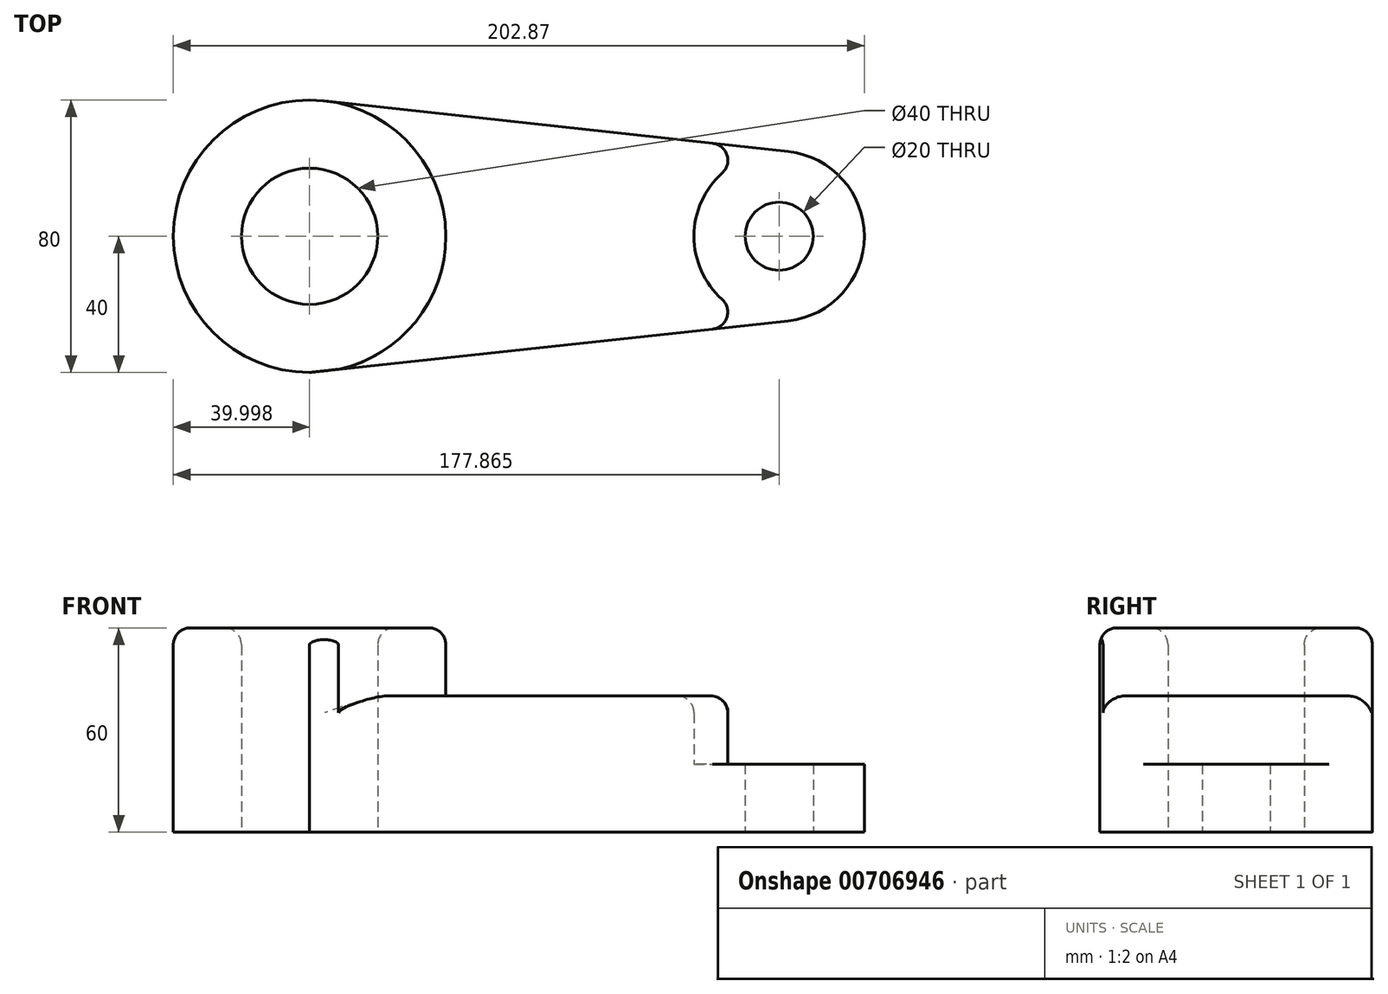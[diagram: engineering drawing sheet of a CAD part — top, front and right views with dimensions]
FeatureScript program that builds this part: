
annotation { "Feature Type Name" : "Feature", "Feature Type Description" : "" }
export const myFeature = defineFeature(function(context is Context, id is Id, definition is map)
    precondition{}
    {
        {
            var Q0;
            Q0=qCreatedBy(makeId("Top.planeOp"),FACE);
            var sketch = newSketch(context, id + "F0", { "sketchPlane" : qUnion([Q0])});
            skCircle(sketch, "E0", {"center": v(-69.3, 0) * mm, "radius": 40 * mm});
            skCircle(sketch, "E1", {"center": v(-69.3, 0) * mm, "radius": 20 * mm});
            skCircle(sketch, "E2", {"center": v(68.58, 0) * mm, "radius": 25 * mm});
            skCircle(sketch, "E3", {"center": v(68.58, 0) * mm, "radius": 10 * mm});
            skLineSegment(sketch, "E4", {"start": v(-64.94, 39.76) * mm, "end": v(71.3, 24.85) * mm});
            skLineSegment(sketch, "E5", {"start": v(-69.3, -40) * mm, "end": v(71.25, -24.86) * mm});
            skSolve(sketch);
        }
        {
            var Q0;
            Q0=makeQuery(id+"F0.imprint","IMPRINT",FACE,{"disambiguationData":[TD([[makeQuery(id+"F0.imprint","IMPRINT",EDGE,{"derivedFrom":sQuery(id+"F0.wireOp",EDGE,"E1")}),-1.0]])]});
            extrude(context, id + "F1", {"entities" : qUnion([Q0]), "depth" : 60 * mm, "offsetDistance" : 25 * mm});
        }
        {
            var Q0;
            {var subQ0=sQuery(id+"F0.wireOp",EDGE,"E4");Q0=makeQuery(id+"F0.imprint","IMPRINT",FACE,{"disambiguationData":[TD([[makeQuery(id+"F0.imprint","IMPRINT",EDGE,{"derivedFrom":subQ0}),-1.0]])]});}
            extrude(context, id + "F2", {"entities" : qUnion([Q0]), "operationType" : NewBodyOperationType.ADD, "depth" : 40 * mm, "offsetDistance" : 25 * mm});
        }
        {
            var Q0;
            Q0=makeQuery(id+"F0.imprint","IMPRINT",FACE,{"disambiguationData":[TD([[makeQuery(id+"F0.imprint","IMPRINT",EDGE,{"derivedFrom":sQuery(id+"F0.wireOp",EDGE,"E3")}),-1.0]])]});
            extrude(context, id + "F3", {"entities" : qUnion([Q0]), "operationType" : NewBodyOperationType.ADD, "depth" : 20 * mm, "offsetDistance" : 25 * mm});
        }
        {
            var Q0;
            Q0=makeQuery(id+"F1.opExtrude","CAP_EDGE",EDGE,{"disambiguationData":[OSD([sQuery(id+"F0.wireOp",EDGE,"E1")])],"isStart":false});
            var Q1;
            Q1=makeQuery(id+"F1.opExtrude","CAP_EDGE",EDGE,{"disambiguationData":[OSD([sQuery(id+"F0.wireOp",EDGE,"E0")])],"isStart":false});
            var Q2;
            Q2=makeQuery(id+"F2.opExtrude","CAP_EDGE",EDGE,{"disambiguationData":[OSD([sQuery(id+"F0.wireOp",EDGE,"E5")])],"isStart":false});
            var Q3;
            Q3=makeQuery(id+"F2.opExtrude","CAP_EDGE",EDGE,{"disambiguationData":[OSD([sQuery(id+"F0.wireOp",EDGE,"E4")])],"isStart":false});
            var Q4;
            Q4=makeQuery(id+"F2.opExtrude","CAP_EDGE",EDGE,{"disambiguationData":[OSD([sQuery(id+"F0.wireOp",EDGE,"E2")])],"isStart":false});
            var Q5;
            {var subQ0=sQuery(id+"F0.wireOp",EDGE,"E5");var subQ1=sQuery(id+"F0.wireOp",EDGE,"E2");Q5=makeQuery(id+"F3.boolean.opBoolean","SPLIT",EDGE,{"disambiguationData":[topologyDisambiguationEdgeConnected([makeQuery(id+"F2.opExtrude","SWEPT_FACE",FACE,{"disambiguationData":[OSD([subQ1])]})])],"derivedFrom":makeQuery(id+"F2.opExtrude","SWEPT_EDGE",EDGE,{"disambiguationData":[OSD([subQ1,subQ0])]})});}
            var Q6;
            {var subQ0=sQuery(id+"F0.wireOp",EDGE,"E2");var subQ1=sQuery(id+"F0.wireOp",EDGE,"E4");Q6=makeQuery(id+"F3.boolean.opBoolean","SPLIT",EDGE,{"disambiguationData":[topologyDisambiguationEdgeConnected([makeQuery(id+"F2.opExtrude","SWEPT_FACE",FACE,{"disambiguationData":[OSD([subQ0])]})])],"derivedFrom":makeQuery(id+"F2.opExtrude","SWEPT_EDGE",EDGE,{"disambiguationData":[OSD([subQ0,subQ1])]})});}
            fillet(context, id + "F4", {"entities" : qUnion([Q0, Q1, Q2, Q3, Q4, Q5, Q6]), "radius" : 5 * mm, "tangentPropagation" : true, "allowEdgeOverflow" : false});
        }
    });
